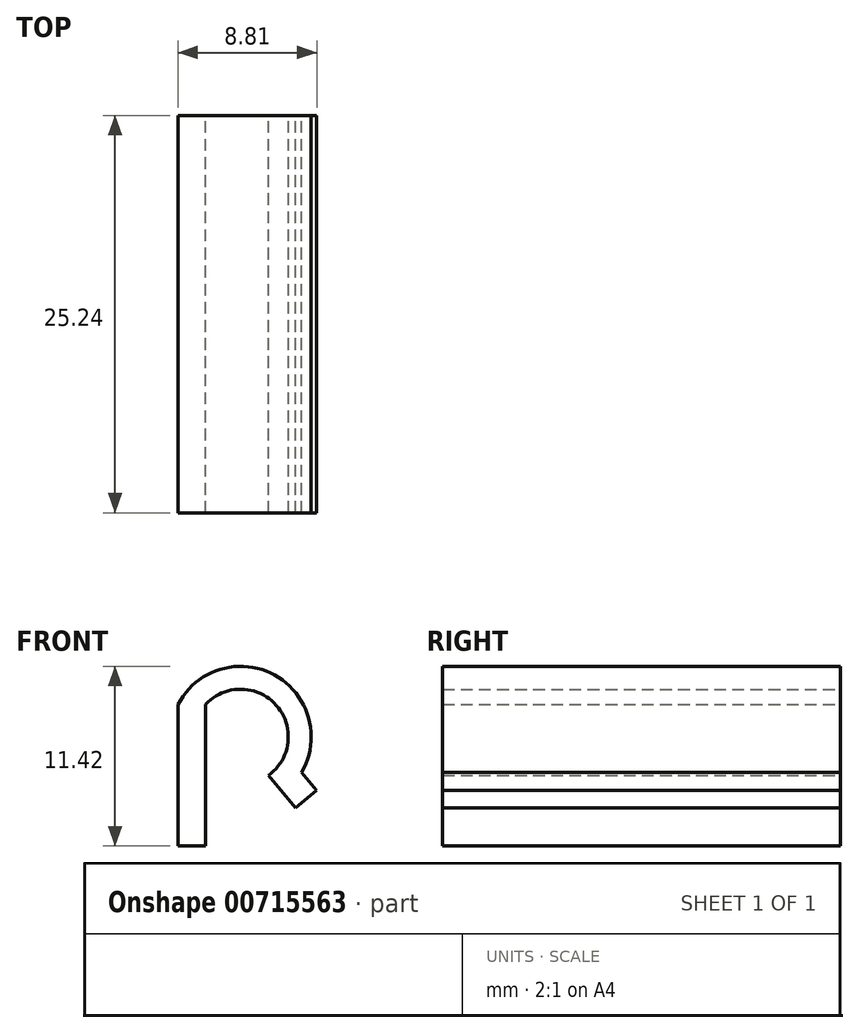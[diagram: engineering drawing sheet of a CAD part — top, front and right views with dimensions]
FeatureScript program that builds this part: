
annotation { "Feature Type Name" : "Feature", "Feature Type Description" : "" }
export const myFeature = defineFeature(function(context is Context, id is Id, definition is map)
    precondition{}
    {
        {
            var Q0;
            Q0=qCreatedBy(makeId("Front.planeOp"),FACE);
            var sketch = newSketch(context, id + "F0", { "sketchPlane" : qUnion([Q0])});
            skLineSegment(sketch, "E0.bottom", {"start": v(0, 0) * mm, "end": v(1.75, 0) * mm});
            skLineSegment(sketch, "E0.left", {"start": v(0, 0) * mm, "end": v(0, 9) * mm});
            skLineSegment(sketch, "E0.right", {"start": v(1.75, 4.49) * mm, "end": v(1.75, 8.99) * mm});
            skArc(sketch, "E1", {"start": v(5.75, 4.49) * mm, "mid": v(6.24, 8.95) * mm, "end": v(1.75, 8.99) * mm});
            skArc(sketch, "E2", {"start": v(7.85, 4.7) * mm, "mid": v(6.13, 10.87) * mm, "end": v(0, 9) * mm});
            skLineSegment(sketch, "E3", {"start": v(1.75, 4.49) * mm, "end": v(1.75, 0) * mm});
            skLineSegment(sketch, "E4", {"start": v(5.75, 4.49) * mm, "end": v(7.46, 2.42) * mm});
            skLineSegment(sketch, "E5", {"start": v(7.46, 2.42) * mm, "end": v(8.8, 3.54) * mm});
            skLineSegment(sketch, "E6", {"start": v(8.8, 3.54) * mm, "end": v(7.85, 4.7) * mm});
            skSolve(sketch);
        }
        {
            var Q0;
            Q0=makeQuery(id+"F0.imprint","IMPRINT",FACE,{"disambiguationData":[TD([[makeQuery(id+"F0.imprint","IMPRINT",EDGE,{"derivedFrom":sQuery(id+"F0.wireOp",EDGE,"E0.bottom")}),1.0]])]});
            extrude(context, id + "F1", {"entities" : qUnion([Q0]), "endBound" : BoundingType.SYMMETRIC, "depth" : 25.25 * mm, "offsetDistance" : 25 * mm});
        }
    });
